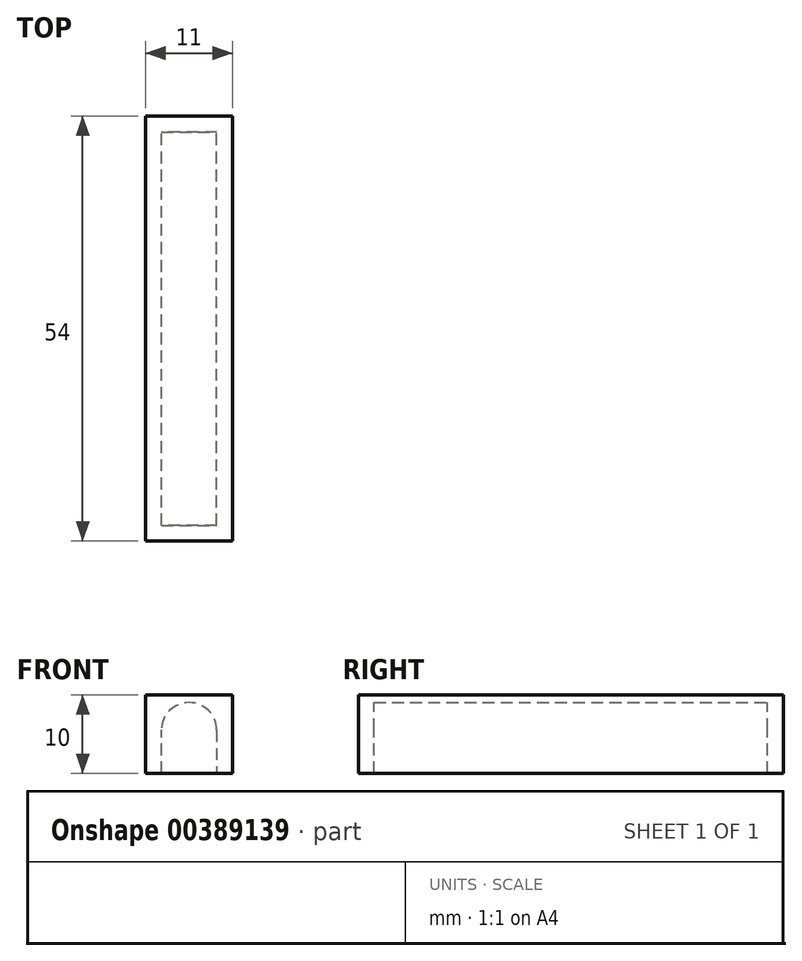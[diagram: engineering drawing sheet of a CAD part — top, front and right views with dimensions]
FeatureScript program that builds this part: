
annotation { "Feature Type Name" : "Feature", "Feature Type Description" : "" }
export const myFeature = defineFeature(function(context is Context, id is Id, definition is map)
    precondition{}
    {
        {
            var Q0;
            Q0=qCreatedBy(makeId("Front.planeOp"),FACE);
            var sketch = newSketch(context, id + "F0", { "sketchPlane" : qUnion([Q0])});
            skLineSegment(sketch, "E0", {"start": v(0, 0) * mm, "end": v(2, 0) * mm});
            skLineSegment(sketch, "E1", {"start": v(2, 0) * mm, "end": v(2, 5.5) * mm});
            skLineSegment(sketch, "E2", {"start": v(2, 5.5) * mm, "end": v(5.5, 5.5) * mm, "construction": true});
            skArc(sketch, "E3", {"start": v(2, 5.5) * mm, "mid": v(5.5, 9) * mm, "end": v(9, 5.5) * mm});
            skLineSegment(sketch, "E4", {"start": v(9, 5.5) * mm, "end": v(9, 0) * mm});
            skLineSegment(sketch, "E5", {"start": v(9, 0) * mm, "end": v(11, 0) * mm});
            skLineSegment(sketch, "E6", {"start": v(11, 0) * mm, "end": v(11, 10) * mm});
            skLineSegment(sketch, "E7", {"start": v(11, 10) * mm, "end": v(0, 10) * mm});
            skLineSegment(sketch, "E8", {"start": v(0, 10) * mm, "end": v(0, 0) * mm});
            skSolve(sketch);
        }
        {
            var Q0;
            Q0 = qSketchRegion(id + "F0", true);
            extrude(context, id + "F1", {"entities" : qUnion([Q0]), "depth" : 50 * mm});
        }
        {
            var Q0;
            Q0=makeQuery(id+"F1.opExtrude","CAP_FACE",FACE,{"disambiguationData":[OSD([sQuery(id+"F0.wireOp",EDGE,"E0"),sQuery(id+"F0.wireOp",EDGE,"E1"),sQuery(id+"F0.wireOp",EDGE,"E3"),sQuery(id+"F0.wireOp",EDGE,"E4"),sQuery(id+"F0.wireOp",EDGE,"E5"),sQuery(id+"F0.wireOp",EDGE,"E6"),sQuery(id+"F0.wireOp",EDGE,"E7"),sQuery(id+"F0.wireOp",EDGE,"E8")])],"isStart":true});
            var sketch = newSketch(context, id + "F2", { "sketchPlane" : qUnion([Q0])});
            skLineSegment(sketch, "E9.bottom", {"start": v(0, 0) * mm, "end": v(-11, 0) * mm});
            skLineSegment(sketch, "E9.top", {"start": v(0, 10) * mm, "end": v(-11, 10) * mm});
            skLineSegment(sketch, "E9.left", {"start": v(0, 0) * mm, "end": v(0, 10) * mm});
            skLineSegment(sketch, "E9.right", {"start": v(-11, 0) * mm, "end": v(-11, 10) * mm});
            skSolve(sketch);
        }
        {
            var Q0;
            Q0 = qSketchRegion(id + "F2", true);
            extrude(context, id + "F3", {"entities" : qUnion([Q0]), "operationType" : NewBodyOperationType.ADD, "depth" : 2 * mm});
        }
        {
            var Q0;
            Q0=makeQuery(id+"F1.opExtrude","CAP_FACE",FACE,{"disambiguationData":[OSD([sQuery(id+"F0.wireOp",EDGE,"E0"),sQuery(id+"F0.wireOp",EDGE,"E1"),sQuery(id+"F0.wireOp",EDGE,"E3"),sQuery(id+"F0.wireOp",EDGE,"E4"),sQuery(id+"F0.wireOp",EDGE,"E5"),sQuery(id+"F0.wireOp",EDGE,"E6"),sQuery(id+"F0.wireOp",EDGE,"E7"),sQuery(id+"F0.wireOp",EDGE,"E8")])],"isStart":false});
            var sketch = newSketch(context, id + "F4", { "sketchPlane" : qUnion([Q0])});
            skLineSegment(sketch, "E10.bottom", {"start": v(0, 0) * mm, "end": v(11, 0) * mm});
            skLineSegment(sketch, "E10.top", {"start": v(0, 10) * mm, "end": v(11, 10) * mm});
            skLineSegment(sketch, "E10.left", {"start": v(0, 0) * mm, "end": v(0, 10) * mm});
            skLineSegment(sketch, "E10.right", {"start": v(11, 0) * mm, "end": v(11, 10) * mm});
            skSolve(sketch);
        }
        {
            var Q0;
            Q0 = qSketchRegion(id + "F4", true);
            extrude(context, id + "F5", {"entities" : qUnion([Q0]), "operationType" : NewBodyOperationType.ADD, "depth" : 2 * mm});
        }
    });
